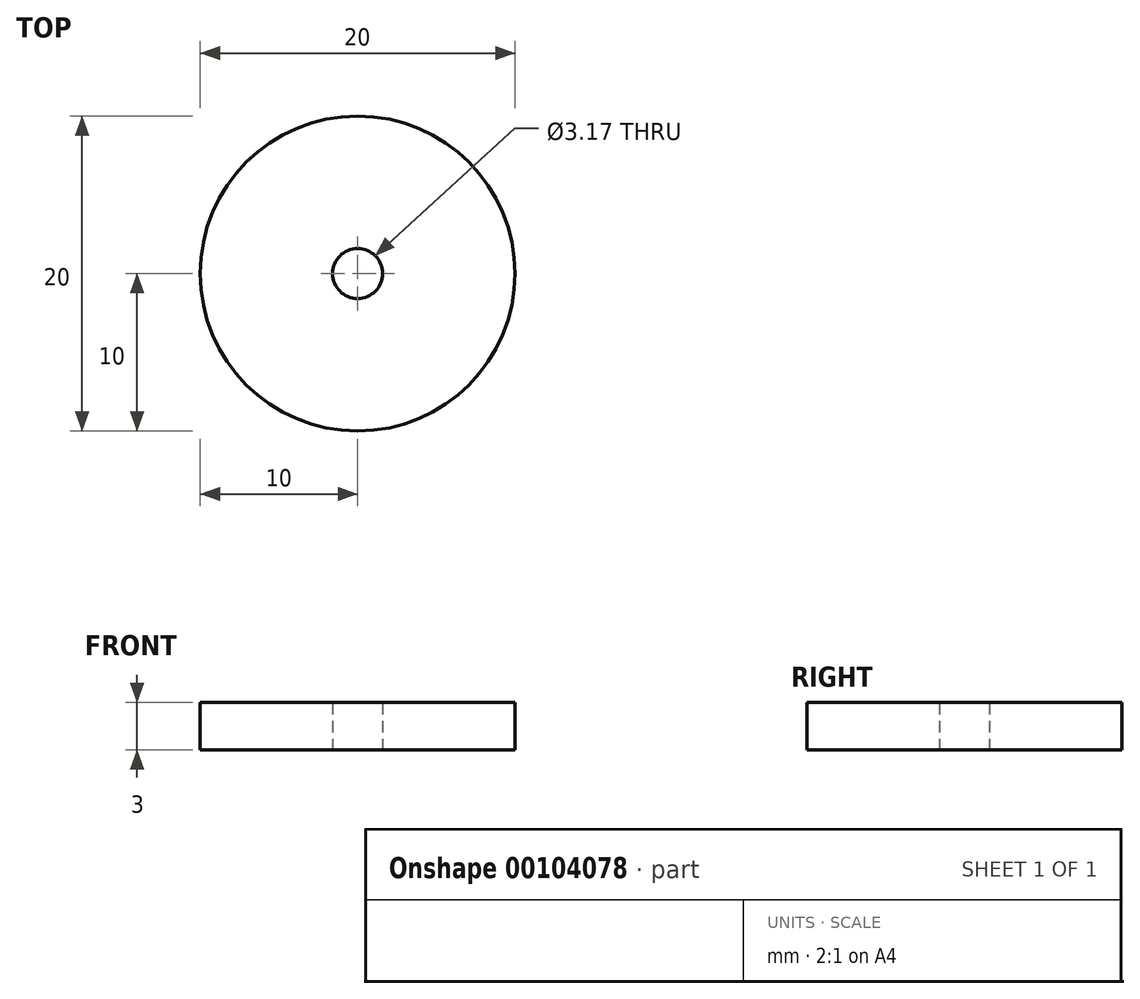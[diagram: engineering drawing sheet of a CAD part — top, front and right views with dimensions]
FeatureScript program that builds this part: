
annotation { "Feature Type Name" : "Feature", "Feature Type Description" : "" }
export const myFeature = defineFeature(function(context is Context, id is Id, definition is map)
    precondition{}
    {
        {
            var Q0;
            Q0=qCreatedBy(makeId("Top.planeOp"),FACE);
            var sketch = newSketch(context, id + "F0", { "sketchPlane" : qUnion([Q0])});
            skCircle(sketch, "E0", {"center": v(-37.42, 18.16) * mm, "radius": 1.59 * mm});
            skCircle(sketch, "E1", {"center": v(-37.42, 18.16) * mm, "radius": 10 * mm});
            skSolve(sketch);
        }
        {
            var Q0;
            Q0=makeQuery(id+"F0.imprint","IMPRINT",FACE,{"disambiguationData":[TD([[makeQuery(id+"F0.imprint","IMPRINT",EDGE,{"derivedFrom":sQuery(id+"F0.wireOp",EDGE,"E0")}),-1.0]])]});
            extrude(context, id + "F1", {"entities" : qUnion([Q0]), "depth" : 3 * mm});
        }
    });
